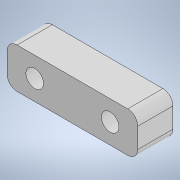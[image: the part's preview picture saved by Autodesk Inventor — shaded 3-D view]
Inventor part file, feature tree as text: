
AUTODESK INVENTOR PART (.ipt)
format: ipt  version: 2022 (Build 260153000, 153)  size: 113,152 bytes
history: native  units: mm
features: extrude x2, sketch x2, fillet x1
ambient origin geometry x8: Origin, YZ Plane, XZ Plane, XY Plane, X Axis, Y Axis, Z Axis, Center Point
bodies: Solid1 (feature_tree)
feature tree (5):
  extrude  "Extrusion1"  Depth=8.0mm
  extrude  "Extrusion2"  Depth=2.0mm
  fillet  "Fillet1"  Radius=15.0mm
  sketch  "Sketch1"  dims[d0=26.0mm d1=8.0mm]
  sketch  "Sketch2"  dims[d2=7.0mm d3=0.0mm d4=3.5mm d5=15.0mm d6=0.0mm d7=0.0mm d8=2.0mm]
